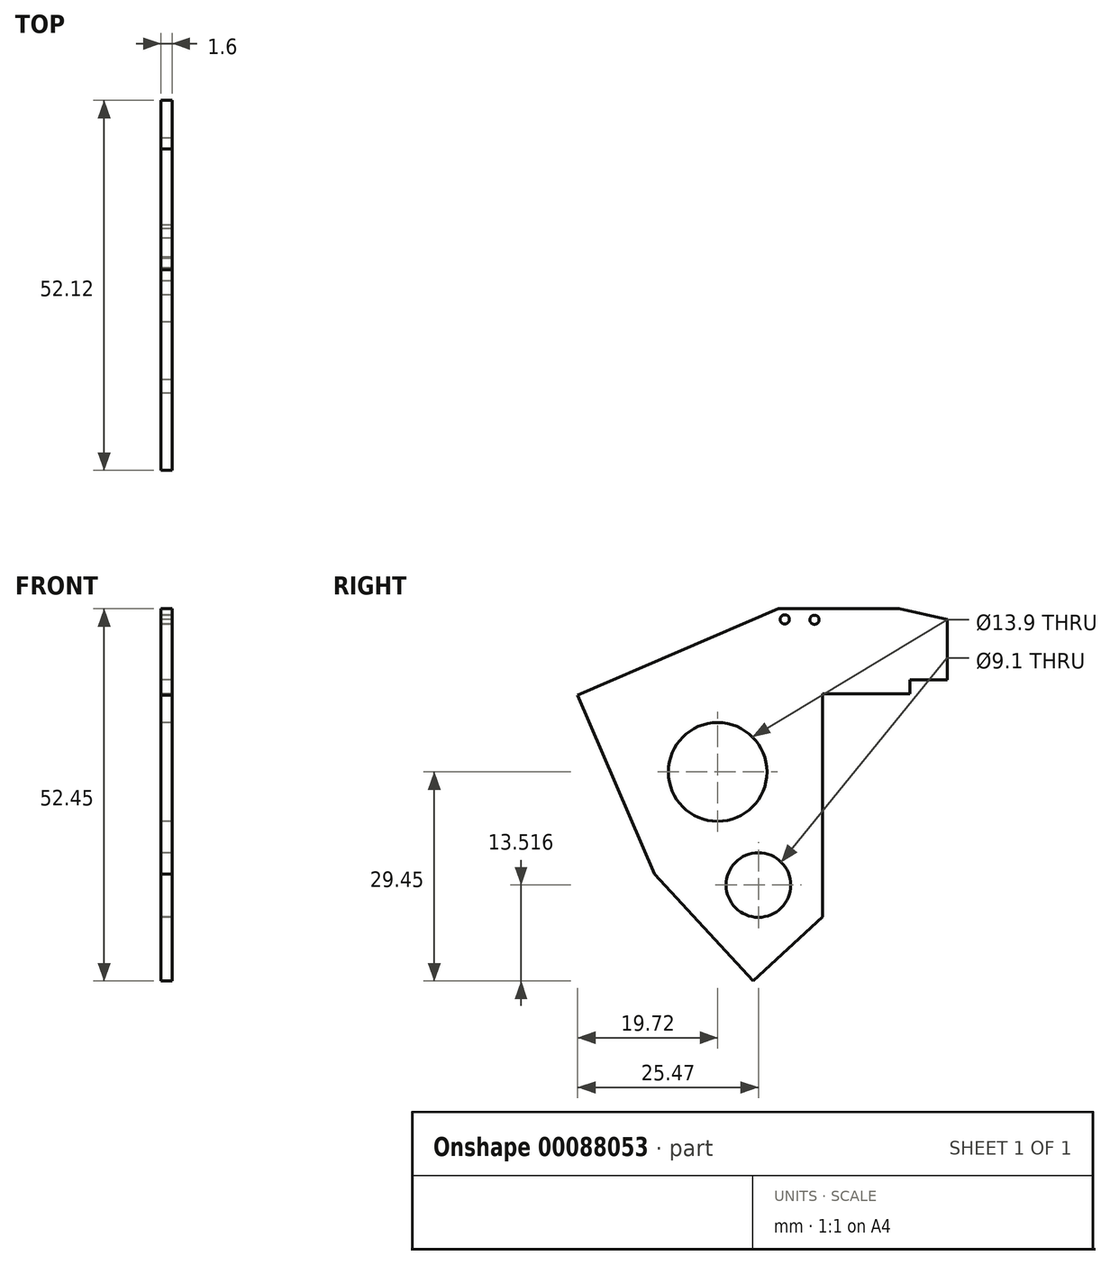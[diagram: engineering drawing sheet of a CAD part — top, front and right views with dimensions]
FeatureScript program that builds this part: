
annotation { "Feature Type Name" : "Feature", "Feature Type Description" : "" }
export const myFeature = defineFeature(function(context is Context, id is Id, definition is map)
    precondition{}
    {
        {
            var Q0;
            Q0=qCreatedBy(makeId("Right.planeOp"),FACE);
            var sketch = newSketch(context, id + "F0", { "sketchPlane" : qUnion([Q0])});
            skCircle(sketch, "E0", {"center": v(0, 0) * mm, "radius": 6.95 * mm});
            skCircle(sketch, "E1", {"center": v(5.75, -15.93) * mm, "radius": 4.55 * mm});
            skLineSegment(sketch, "E2", {"start": v(14.8, -20.45) * mm, "end": v(14.8, 11) * mm});
            skLineSegment(sketch, "E3", {"start": v(14.8, 11) * mm, "end": v(27.1, 11) * mm});
            skLineSegment(sketch, "E4", {"start": v(14.8, -20.45) * mm, "end": v(5.01, -29.45) * mm});
            skLineSegment(sketch, "E5", {"start": v(5.01, -29.45) * mm, "end": v(-8.87, -14.37) * mm});
            skLineSegment(sketch, "E6", {"start": v(-8.87, -14.37) * mm, "end": v(-19.72, 10.8) * mm});
            skLineSegment(sketch, "E7", {"start": v(-19.72, 10.8) * mm, "end": v(8.57, 23) * mm});
            skLineSegment(sketch, "E8", {"start": v(8.57, 23) * mm, "end": v(25.57, 23) * mm});
            skLineSegment(sketch, "E9", {"start": v(25.57, 23) * mm, "end": v(32.4, 21.46) * mm});
            skLineSegment(sketch, "E10", {"start": v(32.4, 21.46) * mm, "end": v(32.4, 13) * mm});
            skLineSegment(sketch, "E11", {"start": v(32.4, 13) * mm, "end": v(27.1, 13) * mm});
            skLineSegment(sketch, "E12", {"start": v(27.1, 13) * mm, "end": v(27.1, 11) * mm});
            skCircle(sketch, "E13", {"center": v(9.46, 21.5) * mm, "radius": 0.65 * mm});
            skCircle(sketch, "E14", {"center": v(13.66, 21.44) * mm, "radius": 0.65 * mm});
            skSolve(sketch);
        }
        {
            var Q0;
            Q0 = qSketchRegion(id + "F0", true);
            extrude(context, id + "F1", {"entities" : qUnion([Q0]), "depth" : 1.6 * mm, "offsetDistance" : 25 * mm});
        }
    });
